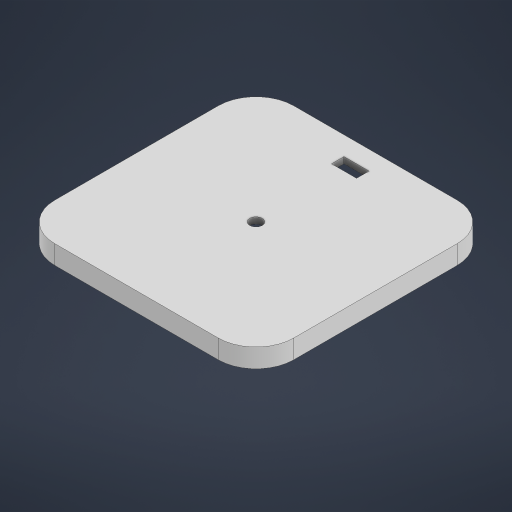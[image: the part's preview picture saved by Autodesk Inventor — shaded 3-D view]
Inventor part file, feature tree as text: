
AUTODESK INVENTOR PART (.ipt)
format: ipt  version: 2024 (Build 280153000, 153)  size: 398,848 bytes
history: native  units: mm
features: extrude x4, sketch x4, other x1, shell x1
ambient origin geometry x8: Origin, YZ Plane, XZ Plane, XY Plane, X Axis, Y Axis, Z Axis, Center Point
bodies: Body1 (feature_tree)
feature tree (10):
  other  "솔리드1"
  extrude  "돌출1"  Depth=190.0mm
  shell  "쉘1"  Thickness=190.0mm
  extrude  "돌출3"  Depth=30.0mm
  extrude  "돌출4"  Depth=15.0mm TaperAngle=0.0deg
  extrude  "돌출5"  Depth=5.0mm
  sketch  "스케치1"
  sketch  "스케치3"
  sketch  "스케치4"
  sketch  "스케치5"
